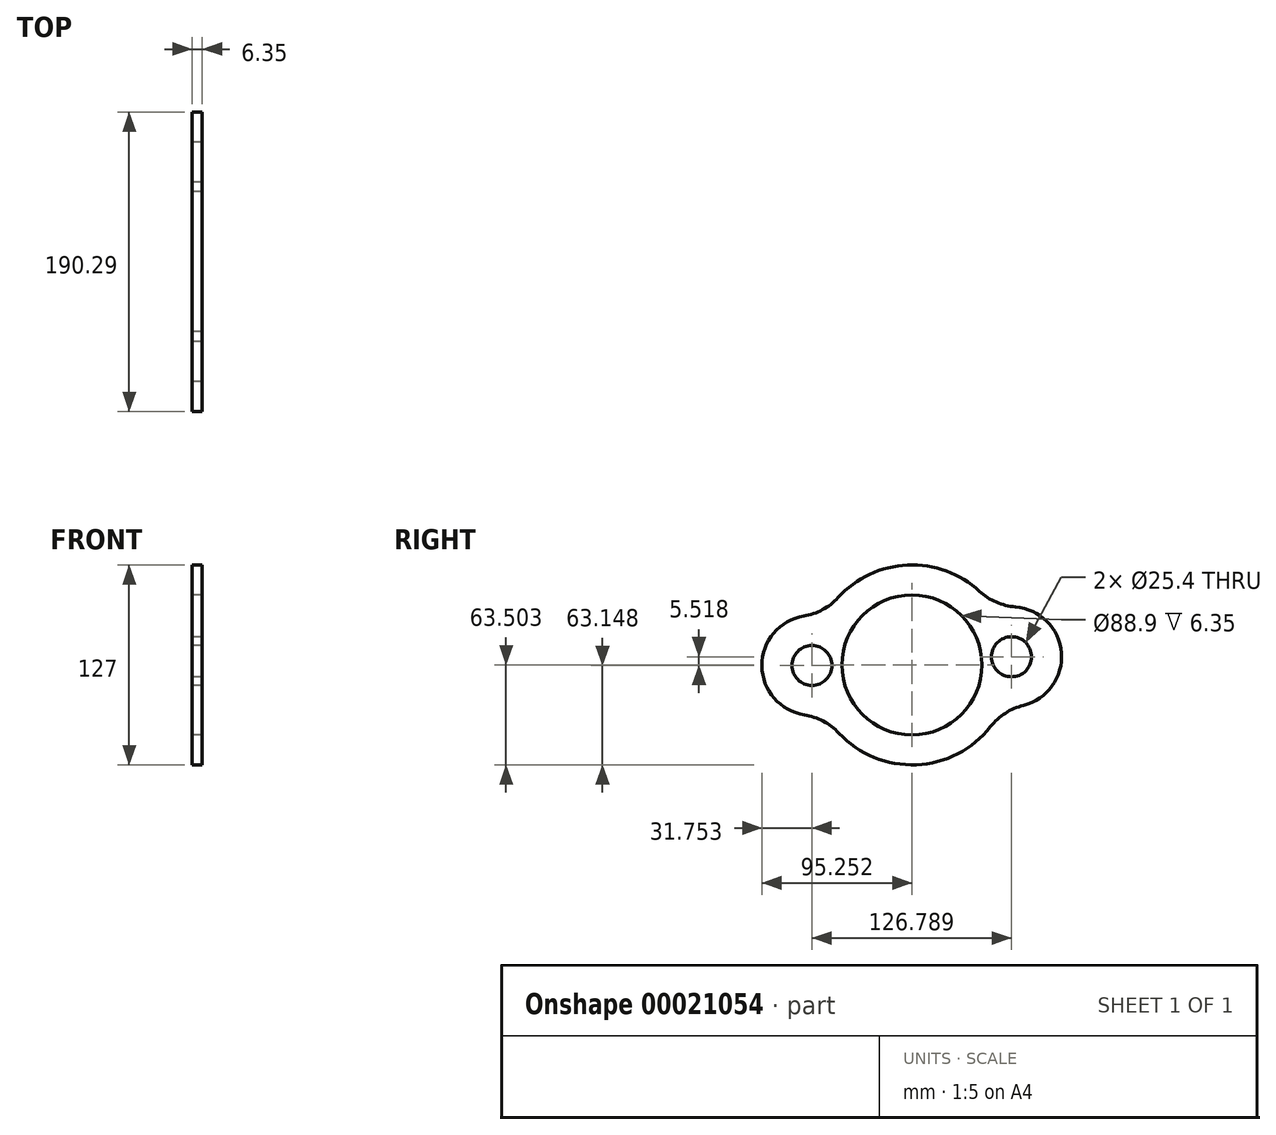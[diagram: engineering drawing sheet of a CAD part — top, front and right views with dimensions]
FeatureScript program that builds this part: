
annotation { "Feature Type Name" : "Feature", "Feature Type Description" : "" }
export const myFeature = defineFeature(function(context is Context, id is Id, definition is map)
    precondition{}
    {
        {
            var Q0;
            Q0=qCreatedBy(makeId("Right.planeOp"),FACE);
            var sketch = newSketch(context, id + "F0", { "sketchPlane" : qUnion([Q0])});
            skArc(sketch, "E0", {"start": v(-46.86, -43.44) * mm, "mid": v(2.3, -63.52) * mm, "end": v(49.52, -39.24) * mm});
            skArc(sketch, "E1", {"start": v(-63.97, -0.38) * mm, "mid": v(-63.97, -0.4) * mm, "end": v(-63.97, -0.43) * mm});
            skCircle(sketch, "E2", {"center": v(-0.47, -0.08) * mm, "radius": 44.45 * mm});
            skArc(sketch, "E3", {"start": v(70.4, -25.74) * mm, "mid": v(94.47, 7.67) * mm, "end": v(65.3, 36.74) * mm});
            skCircle(sketch, "E4", {"center": v(62.82, 5.09) * mm, "radius": 12.7 * mm});
            skArc(sketch, "E5", {"start": v(-69.2, 30.89) * mm, "mid": v(-95.72, -0.6) * mm, "end": v(-68.84, -31.8) * mm});
            skCircle(sketch, "E6", {"center": v(-63.97, -0.43) * mm, "radius": 12.7 * mm});
            skArc(sketch, "E7.trimOffspring", {"start": v(42.5, 46.67) * mm, "mid": v(-3.23, 63.36) * mm, "end": v(-47.34, 42.76) * mm});
            skPoint(sketch, "E8.visualSharp", {"position": v(52.41, 35.08) * mm});
            skArc(sketch, "E8.filletArc", {"start": v(42.5, 46.67) * mm, "mid": v(53.07, 39.8) * mm, "end": v(65.3, 36.74) * mm});
            skPoint(sketch, "E9.visualSharp", {"position": v(57.41, -26.2) * mm});
            skArc(sketch, "E9.filletArc", {"start": v(70.4, -25.74) * mm, "mid": v(58.83, -30.74) * mm, "end": v(49.52, -39.24) * mm});
            skPoint(sketch, "E10.visualSharp", {"position": v(-55.86, -31.13) * mm});
            skArc(sketch, "E10.filletArc", {"start": v(-46.86, -43.44) * mm, "mid": v(-56.88, -35.78) * mm, "end": v(-68.84, -31.8) * mm});
            skPoint(sketch, "E11.visualSharp", {"position": v(-56.2, 30.35) * mm});
            skArc(sketch, "E11.filletArc", {"start": v(-69.2, 30.89) * mm, "mid": v(-57.27, 35) * mm, "end": v(-47.34, 42.76) * mm});
            skSolve(sketch);
        }
        {
            var Q0;
            Q0=makeQuery(id+"F0.imprint","IMPRINT",FACE,{"disambiguationData":[TD([[makeQuery(id+"F0.imprint","IMPRINT",EDGE,{"derivedFrom":sQuery(id+"F0.wireOp",EDGE,"E0")}),1.0]])]});
            extrude(context, id + "F1", {"entities" : qUnion([Q0]), "depth" : 6.35 * mm});
        }
    });
